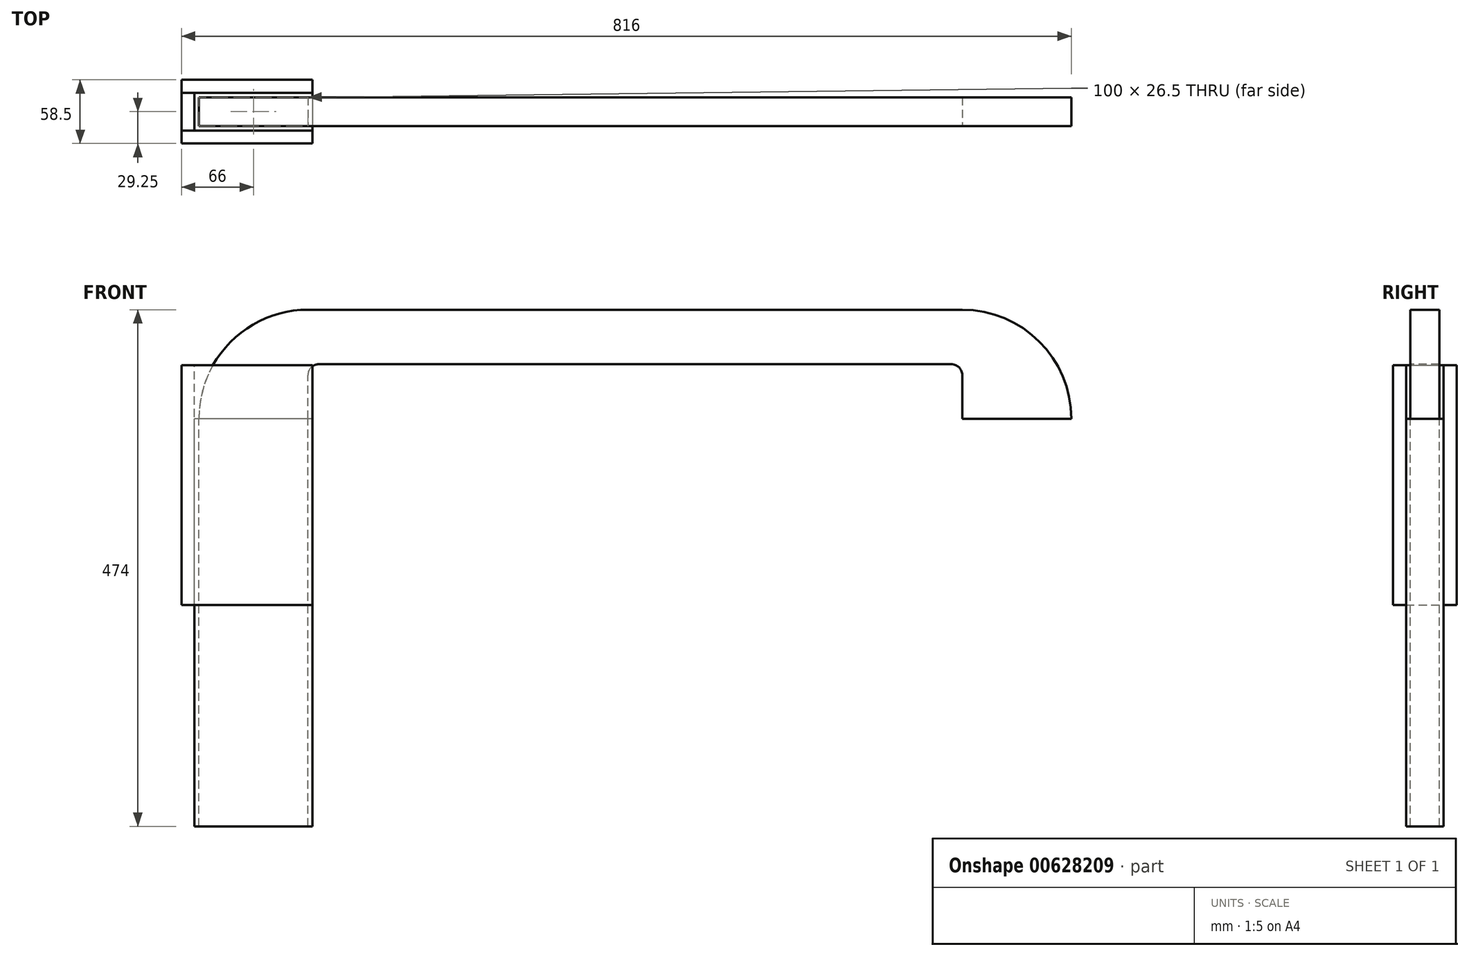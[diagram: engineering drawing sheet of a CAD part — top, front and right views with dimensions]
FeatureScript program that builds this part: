
annotation { "Feature Type Name" : "Feature", "Feature Type Description" : "" }
export const myFeature = defineFeature(function(context is Context, id is Id, definition is map)
    precondition{}
    {
        {
            var Q0;
            Q0=qCreatedBy(makeId("Right.planeOp"),FACE);
            var sketch = newSketch(context, id + "F0", { "sketchPlane" : qUnion([Q0])});
            skLineSegment(sketch, "E0.0", {"start": v(-59.75, -9.5) * mm, "end": v(-33.25, -9.5) * mm});
            skLineSegment(sketch, "E1", {"start": v(-33.25, 90.5) * mm, "end": v(-59.75, 90.5) * mm});
            skLineSegment(sketch, "E2", {"start": v(-59.75, -9.5) * mm, "end": v(-59.75, 90.5) * mm});
            skPoint(sketch, "E3.orphan", {"position": v(-20.25, 247.25) * mm});
            skLineSegment(sketch, "E4", {"start": v(-33.25, -9.5) * mm, "end": v(-33.25, 90.5) * mm});
            skSolve(sketch);
        }
        {
            var Q0;
            Q0=makeQuery(id+"F0.imprint","IMPRINT",FACE,{"disambiguationData":[TD([[makeQuery(id+"F0.imprint","IMPRINT",EDGE,{"derivedFrom":sQuery(id+"F0.wireOp",EDGE,"E0.0")}),1.0]])]});
            extrude(context, id + "F1", {"entities" : qUnion([Q0]), "depth" : 400 * mm, "offsetDistance" : 25 * mm, "hasSecondDirection" : true, "secondDirectionOppositeDirection" : true, "secondDirectionDepth" : 400 * mm});
        }
        {
            var Q0;
            Q0=makeQuery(id+"F1.opExtrude","SWEPT_FACE",FACE,{"disambiguationData":[OSD([sQuery(id+"F0.wireOp",EDGE,"E2")])]});
            var sketch = newSketch(context, id + "F2", { "sketchPlane" : qUnion([Q0])});
            skLineSegment(sketch, "E5.bottom", {"start": v(-300, -9.5) * mm, "end": v(300, -9.5) * mm});
            skLineSegment(sketch, "E5.top", {"start": v(-300, 40.5) * mm, "end": v(300, 40.5) * mm});
            skLineSegment(sketch, "E5.left", {"start": v(-300, -9.5) * mm, "end": v(-300, 40.5) * mm});
            skLineSegment(sketch, "E5.right", {"start": v(300, -9.5) * mm, "end": v(300, 40.5) * mm});
            skSolve(sketch);
        }
        {
            var Q0;
            Q0=makeQuery(id+"F2.imprint","IMPRINT",FACE,{"disambiguationData":[TD([[makeQuery(id+"F2.imprint","IMPRINT",EDGE,{"derivedFrom":sQuery(id+"F2.wireOp",EDGE,"E5.bottom")}),-1.0]])]});
            extrude(context, id + "F3", {"entities" : qUnion([Q0]), "operationType" : NewBodyOperationType.REMOVE, "endBound" : BoundingType.THROUGH_ALL, "oppositeDirection" : true, "depth" : 25 * mm, "offsetDistance" : 25 * mm});
        }
        {
            var Q0;
            Q0=makeQuery(id+"F1.opExtrude","CAP_EDGE",EDGE,{"disambiguationData":[OSD([sQuery(id+"F0.wireOp",EDGE,"E1")])],"isStart":true});
            var Q1;
            Q1=makeQuery(id+"F1.opExtrude","CAP_EDGE",EDGE,{"disambiguationData":[OSD([sQuery(id+"F0.wireOp",EDGE,"E1")])],"isStart":false});
            fillet(context, id + "F4", {"entities" : qUnion([Q0, Q1]), "radius" : 100 * mm, "tangentPropagation" : true, "allowEdgeOverflow" : false});
        }
        {
            var Q0;
            Q0=makeQuery(id+"F3.boolean.opBoolean","COPY",EDGE,{"derivedFrom":makeQuery(id+"F3.opExtrude","SWEPT_EDGE",EDGE,{"disambiguationData":[OSD([sQuery(id+"F2.wireOp",EDGE,"E5.top"),sQuery(id+"F2.wireOp",EDGE,"E5.left")])]})});
            var Q1;
            Q1=makeQuery(id+"F3.boolean.opBoolean","COPY",EDGE,{"derivedFrom":makeQuery(id+"F3.opExtrude","SWEPT_EDGE",EDGE,{"disambiguationData":[OSD([sQuery(id+"F2.wireOp",EDGE,"E5.top"),sQuery(id+"F2.wireOp",EDGE,"E5.right")])]})});
            fillet(context, id + "F5", {"entities" : qUnion([Q0, Q1]), "radius" : 10 * mm, "tangentPropagation" : true, "allowEdgeOverflow" : false});
        }
        {
            var Q0;
            {var subQ2=sQuery(id+"F0.wireOp",EDGE,"E0.0");Q0=makeQuery(id+"F3.boolean.opBoolean","SPLIT",FACE,{"disambiguationData":[TD([makeQuery(id+"F3.opExtrude","SWEPT_FACE",FACE,{"disambiguationData":[OSD([sQuery(id+"F2.wireOp",EDGE,"E5.left")])]})])],"derivedFrom":makeQuery(id+"F1.opExtrude","SWEPT_FACE",FACE,{"disambiguationData":[OSD([subQ2])]})});}
            var sketch = newSketch(context, id + "F6", { "sketchPlane" : qUnion([Q0])});
            skLineSegment(sketch, "E6.0", {"start": v(-296, 63.75) * mm, "end": v(-404, 63.75) * mm});
            skLineSegment(sketch, "E6.1", {"start": v(-296, 29.25) * mm, "end": v(-296, 63.75) * mm});
            skLineSegment(sketch, "E6.2", {"start": v(-296, 29.25) * mm, "end": v(-404, 29.25) * mm});
            skLineSegment(sketch, "E6.3", {"start": v(-404, 63.75) * mm, "end": v(-404, 29.25) * mm});
            skLineSegment(sketch, "E7", {"start": v(-296, 63.75) * mm, "end": v(-296, 75.75) * mm});
            skLineSegment(sketch, "E8", {"start": v(-296, 75.75) * mm, "end": v(-416, 75.75) * mm});
            skLineSegment(sketch, "E9", {"start": v(-416, 75.75) * mm, "end": v(-416, 17.25) * mm});
            skLineSegment(sketch, "E10", {"start": v(-416, 17.25) * mm, "end": v(-296, 17.25) * mm});
            skLineSegment(sketch, "E11", {"start": v(-296, 17.25) * mm, "end": v(-296, 29.25) * mm});
            skLineSegment(sketch, "E12", {"start": v(-404, 63.75) * mm, "end": v(-416, 63.75) * mm});
            skLineSegment(sketch, "E13", {"start": v(-404, 29.25) * mm, "end": v(-416, 29.25) * mm});
            skSolve(sketch);
        }
        {
            var Q0;
            Q0=makeQuery(id+"F6.imprint","IMPRINT",FACE,{"disambiguationData":[TD([[makeQuery(id+"F6.imprint","IMPRINT",EDGE,{"derivedFrom":sQuery(id+"F6.wireOp",EDGE,"E6.0")}),1.0]])]});
            var Q1;
            {var subQ0=sQuery(id+"F2.wireOp",EDGE,"E5.left");var subQ1=sQuery(id+"F0.wireOp",EDGE,"E2");var subQ2=sQuery(id+"F0.wireOp",EDGE,"E0.0");Q1=makeQuery(id+"F6.imprint","IMPRINT",FACE,{"disambiguationData":[TD([[makeQuery(id+"F6.imprint","IMPRINT",EDGE,{"derivedFrom":makeQuery(id+"F3.boolean.opBoolean","COPY",EDGE,{"derivedFrom":makeQuery(id+"F3.opExtrude","SWEPT_EDGE",EDGE,{"disambiguationData":[OSD([subQ2,subQ1,sQuery(id+"F2.wireOp",EDGE,"E5.bottom"),subQ0])]})})}),1.0]])]});}
            extrude(context, id + "F7", {"entities" : qUnion([Q0, Q1]), "depth" : 374 * mm, "offsetDistance" : 25 * mm});
        }
        {
            var Q0;
            Q0=makeQuery(id+"F6.imprint","IMPRINT",FACE,{"disambiguationData":[TD([[makeQuery(id+"F6.imprint","IMPRINT",EDGE,{"derivedFrom":sQuery(id+"F6.wireOp",EDGE,"E6.0")}),-1.0]])]});
            var Q1;
            Q1=makeQuery(id+"F6.imprint","IMPRINT",FACE,{"disambiguationData":[TD([[makeQuery(id+"F6.imprint","IMPRINT",EDGE,{"derivedFrom":sQuery(id+"F6.wireOp",EDGE,"E6.2")}),1.0]])]});
            extrude(context, id + "F8", {"entities" : qUnion([Q0, Q1]), "depth" : 171 * mm, "offsetDistance" : 25 * mm, "hasSecondDirection" : true, "secondDirectionOppositeDirection" : true, "secondDirectionDepth" : 49 * mm});
        }
        {
            var Q0;
            Q0=makeQuery(id+"F6.imprint","IMPRINT",FACE,{"disambiguationData":[TD([[makeQuery(id+"F6.imprint","IMPRINT",EDGE,{"derivedFrom":sQuery(id+"F6.wireOp",EDGE,"E6.3")}),-1.0]])]});
            var Q1;
            Q1=makeQuery(id+"F8.opExtrude","CAP_FACE",FACE,{"disambiguationData":[OSD([sQuery(id+"F6.wireOp",EDGE,"E6.0"),sQuery(id+"F6.wireOp",EDGE,"E7"),sQuery(id+"F6.wireOp",EDGE,"E8"),sQuery(id+"F6.wireOp",EDGE,"E9"),sQuery(id+"F6.wireOp",EDGE,"E12")])],"isStart":false});
            var Q2;
            Q2=makeQuery(id+"F8.opExtrude","CAP_FACE",FACE,{"disambiguationData":[OSD([sQuery(id+"F6.wireOp",EDGE,"E6.0"),sQuery(id+"F6.wireOp",EDGE,"E7"),sQuery(id+"F6.wireOp",EDGE,"E8"),sQuery(id+"F6.wireOp",EDGE,"E9"),sQuery(id+"F6.wireOp",EDGE,"E12")])],"isStart":true});
            extrude(context, id + "F9", {"entities" : qUnion([Q0]), "endBound" : BoundingType.UP_TO_SURFACE, "depth" : 25 * mm, "endBoundEntityFace" : qUnion([Q1]), "offsetDistance" : 25 * mm, "hasSecondDirection" : true, "secondDirectionBound" : SecondDirectionBoundingType.UP_TO_SURFACE, "secondDirectionOppositeDirection" : true, "secondDirectionDepth" : 25 * mm, "secondDirectionBoundEntityFace" : qUnion([Q2])});
        }
    });
